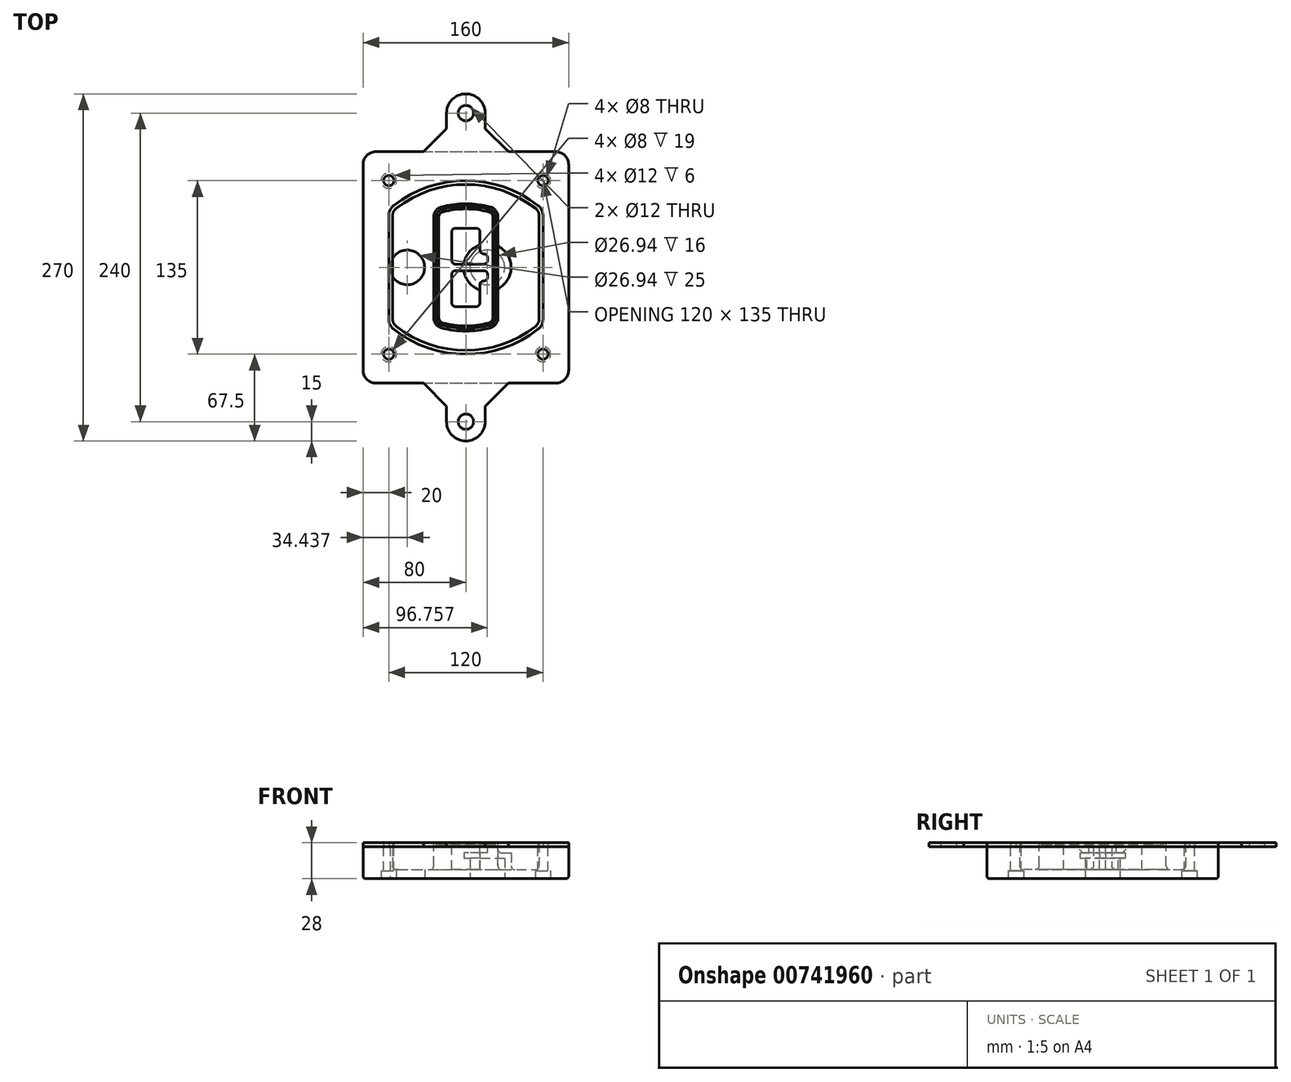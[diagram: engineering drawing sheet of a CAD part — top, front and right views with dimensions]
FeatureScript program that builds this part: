
annotation { "Feature Type Name" : "Feature", "Feature Type Description" : "" }
export const myFeature = defineFeature(function(context is Context, id is Id, definition is map)
    precondition{}
    {
        {
            var Q0;
            Q0=qCreatedBy(makeId("Top.planeOp"),FACE);
            var sketch = newSketch(context, id + "F0", { "sketchPlane" : qUnion([Q0])});
            skPoint(sketch, "E0.rect.middle", {"position": v(0, 0) * mm});
            skLineSegment(sketch, "E1.bottom", {"start": v(-70, -90) * mm, "end": v(70, -90) * mm});
            skLineSegment(sketch, "E1.top", {"start": v(-70, 90) * mm, "end": v(70, 90) * mm});
            skLineSegment(sketch, "E1.left", {"start": v(-80, -80) * mm, "end": v(-80, 80) * mm});
            skLineSegment(sketch, "E1.right", {"start": v(80, -80) * mm, "end": v(80, 80) * mm});
            skLineSegment(sketch, "E2", {"start": v(-80, 90) * mm, "end": v(80, -90) * mm, "construction": true});
            skLineSegment(sketch, "E3", {"start": v(80, 90) * mm, "end": v(-80, -90) * mm, "construction": true});
            skCircle(sketch, "E4", {"center": v(-60, 67.5) * mm, "radius": 4 * mm});
            skCircle(sketch, "E5", {"center": v(60, 67.5) * mm, "radius": 4 * mm});
            skCircle(sketch, "E6", {"center": v(60, -67.5) * mm, "radius": 4 * mm});
            skCircle(sketch, "E7", {"center": v(-60, -67.5) * mm, "radius": 4 * mm});
            skLineSegment(sketch, "E8", {"start": v(-60, 67.5) * mm, "end": v(60, 67.5) * mm, "construction": true});
            skLineSegment(sketch, "E9", {"start": v(60, 67.5) * mm, "end": v(60, -67.5) * mm, "construction": true});
            skLineSegment(sketch, "E10", {"start": v(60, -67.5) * mm, "end": v(-60, -67.5) * mm, "construction": true});
            skLineSegment(sketch, "E11", {"start": v(-60, -67.5) * mm, "end": v(-60, 67.5) * mm, "construction": true});
            skLineSegment(sketch, "E12", {"start": v(-60, 40.3) * mm, "end": v(-60, -40.3) * mm});
            skLineSegment(sketch, "E13", {"start": v(60, 40.3) * mm, "end": v(60, -40.3) * mm});
            skArc(sketch, "E14", {"start": v(56.15, 48.18) * mm, "mid": v(0, 67.5) * mm, "end": v(-56.15, 48.18) * mm});
            skArc(sketch, "E15", {"start": v(-56.15, -48.18) * mm, "mid": v(0, -67.5) * mm, "end": v(56.15, -48.18) * mm});
            skLineSegment(sketch, "E16", {"start": v(-60, 0) * mm, "end": v(60, 0) * mm, "construction": true});
            skPoint(sketch, "E17.visualSharp", {"position": v(-60, -45) * mm});
            skArc(sketch, "E17.filletArc", {"start": v(-60, -40.3) * mm, "mid": v(-58.99, -44.68) * mm, "end": v(-56.15, -48.18) * mm});
            skPoint(sketch, "E18.visualSharp", {"position": v(-60, 45) * mm});
            skArc(sketch, "E18.filletArc", {"start": v(-56.15, 48.18) * mm, "mid": v(-58.99, 44.68) * mm, "end": v(-60, 40.3) * mm});
            skPoint(sketch, "E19.visualSharp", {"position": v(60, 45) * mm});
            skArc(sketch, "E19.filletArc", {"start": v(60, 40.3) * mm, "mid": v(58.99, 44.68) * mm, "end": v(56.15, 48.18) * mm});
            skPoint(sketch, "E20.visualSharp", {"position": v(60, -45) * mm});
            skArc(sketch, "E20.filletArc", {"start": v(56.15, -48.18) * mm, "mid": v(58.99, -44.68) * mm, "end": v(60, -40.3) * mm});
            skPoint(sketch, "E21.visualSharp", {"position": v(-80, 90) * mm});
            skArc(sketch, "E21.filletArc", {"start": v(-70, 90) * mm, "mid": v(-77.07, 87.07) * mm, "end": v(-80, 80) * mm});
            skPoint(sketch, "E22.visualSharp", {"position": v(80, 90) * mm});
            skArc(sketch, "E22.filletArc", {"start": v(80, 80) * mm, "mid": v(77.07, 87.07) * mm, "end": v(70, 90) * mm});
            skPoint(sketch, "E23.visualSharp", {"position": v(80, -90) * mm});
            skArc(sketch, "E23.filletArc", {"start": v(70, -90) * mm, "mid": v(77.07, -87.07) * mm, "end": v(80, -80) * mm});
            skPoint(sketch, "E24.visualSharp", {"position": v(-80, -90) * mm});
            skArc(sketch, "E24.filletArc", {"start": v(-80, -80) * mm, "mid": v(-77.07, -87.07) * mm, "end": v(-70, -90) * mm});
            skArc(sketch, "E25.0", {"start": v(57, 40.3) * mm, "mid": v(56.3, 43.36) * mm, "end": v(54.3, 45.81) * mm});
            skLineSegment(sketch, "E25.1", {"start": v(57, 40.3) * mm, "end": v(57, -40.3) * mm});
            skArc(sketch, "E25.2", {"start": v(54.3, -45.81) * mm, "mid": v(56.3, -43.36) * mm, "end": v(57, -40.3) * mm});
            skArc(sketch, "E25.3", {"start": v(-54.3, -45.81) * mm, "mid": v(0, -64.5) * mm, "end": v(54.3, -45.81) * mm});
            skArc(sketch, "E25.4", {"start": v(-57, -40.3) * mm, "mid": v(-56.3, -43.36) * mm, "end": v(-54.3, -45.81) * mm});
            skArc(sketch, "E25.5", {"start": v(54.3, 45.81) * mm, "mid": v(0, 64.5) * mm, "end": v(-54.3, 45.81) * mm});
            skLineSegment(sketch, "E25.6", {"start": v(-57, 40.3) * mm, "end": v(-57, -40.3) * mm});
            skArc(sketch, "E25.7", {"start": v(-54.3, 45.81) * mm, "mid": v(-56.3, 43.36) * mm, "end": v(-57, 40.3) * mm});
            skArc(sketch, "E26.0", {"start": v(-58.62, 51.33) * mm, "mid": v(-62.58, 46.43) * mm, "end": v(-64, 40.3) * mm});
            skArc(sketch, "E26.1", {"start": v(58.62, 51.33) * mm, "mid": v(0, 71.5) * mm, "end": v(-58.62, 51.33) * mm});
            skArc(sketch, "E26.2", {"start": v(64, 40.3) * mm, "mid": v(62.58, 46.43) * mm, "end": v(58.62, 51.33) * mm});
            skLineSegment(sketch, "E26.3", {"start": v(64, 40.3) * mm, "end": v(64, -40.3) * mm});
            skArc(sketch, "E26.4", {"start": v(58.62, -51.33) * mm, "mid": v(62.58, -46.43) * mm, "end": v(64, -40.3) * mm});
            skLineSegment(sketch, "E26.5", {"start": v(-64, 40.3) * mm, "end": v(-64, -40.3) * mm});
            skArc(sketch, "E26.6", {"start": v(-58.62, -51.33) * mm, "mid": v(0, -71.5) * mm, "end": v(58.62, -51.33) * mm});
            skArc(sketch, "E26.7", {"start": v(-64, -40.3) * mm, "mid": v(-62.58, -46.43) * mm, "end": v(-58.62, -51.33) * mm});
            skSolve(sketch);
        }
        {
            var Q0;
            Q0=makeQuery(id+"F0.imprint","IMPRINT",FACE,{"disambiguationData":[TD([[makeQuery(id+"F0.imprint","IMPRINT",EDGE,{"derivedFrom":sQuery(id+"F0.wireOp",EDGE,"E1.bottom")}),1.0]])]});
            var Q1;
            Q1=makeQuery(id+"F0.imprint","IMPRINT",FACE,{"disambiguationData":[TD([[makeQuery(id+"F0.imprint","IMPRINT",EDGE,{"derivedFrom":sQuery(id+"F0.wireOp",EDGE,"E12")}),1.0]])]});
            var Q2;
            Q2=makeQuery(id+"F0.imprint","IMPRINT",FACE,{"disambiguationData":[TD([[makeQuery(id+"F0.imprint","IMPRINT",EDGE,{"derivedFrom":sQuery(id+"F0.wireOp",EDGE,"E25.0")}),1.0]])]});
            var Q3;
            Q3=makeQuery(id+"F0.imprint","IMPRINT",FACE,{"disambiguationData":[TD([[makeQuery(id+"F0.imprint","IMPRINT",EDGE,{"derivedFrom":sQuery(id+"F0.wireOp",EDGE,"E12")}),-1.0]])]});
            extrude(context, id + "F1", {"entities" : qUnion([Q0, Q1, Q2, Q3]), "oppositeDirection" : true, "depth" : 25 * mm});
        }
        {
            var Q0;
            Q0=makeQuery(id+"F0.imprint","IMPRINT",FACE,{"disambiguationData":[TD([[makeQuery(id+"F0.imprint","IMPRINT",EDGE,{"derivedFrom":sQuery(id+"F0.wireOp",EDGE,"E12")}),1.0]])]});
            extrude(context, id + "F2", {"entities" : qUnion([Q0]), "operationType" : NewBodyOperationType.ADD, "depth" : 3 * mm});
        }
        {
            var Q0;
            Q0=makeQuery(id+"F0.imprint","IMPRINT",FACE,{"disambiguationData":[TD([[makeQuery(id+"F0.imprint","IMPRINT",EDGE,{"derivedFrom":sQuery(id+"F0.wireOp",EDGE,"E25.0")}),1.0]])]});
            extrude(context, id + "F3", {"entities" : qUnion([Q0]), "operationType" : NewBodyOperationType.REMOVE, "oppositeDirection" : true, "depth" : 18 * mm});
        }
        {
            var Q0;
            Q0=makeQuery(id+"F2.opExtrude","CAP_FACE",FACE,{"disambiguationData":[OSD([sQuery(id+"F0.wireOp",EDGE,"E12"),sQuery(id+"F0.wireOp",EDGE,"E13"),sQuery(id+"F0.wireOp",EDGE,"E14"),sQuery(id+"F0.wireOp",EDGE,"E15"),sQuery(id+"F0.wireOp",EDGE,"E17.filletArc"),sQuery(id+"F0.wireOp",EDGE,"E18.filletArc"),sQuery(id+"F0.wireOp",EDGE,"E19.filletArc"),sQuery(id+"F0.wireOp",EDGE,"E20.filletArc"),sQuery(id+"F0.wireOp",EDGE,"E25.0"),sQuery(id+"F0.wireOp",EDGE,"E25.1"),sQuery(id+"F0.wireOp",EDGE,"E25.2"),sQuery(id+"F0.wireOp",EDGE,"E25.3"),sQuery(id+"F0.wireOp",EDGE,"E25.4"),sQuery(id+"F0.wireOp",EDGE,"E25.5"),sQuery(id+"F0.wireOp",EDGE,"E25.6"),sQuery(id+"F0.wireOp",EDGE,"E25.7")])],"isStart":false});
            var sketch = newSketch(context, id + "F4", { "sketchPlane" : qUnion([Q0])});
            skArc(sketch, "E27.0", {"start": v(-19.08, -46.97) * mm, "mid": v(0, -49.5) * mm, "end": v(19.08, -46.97) * mm});
            skArc(sketch, "E28.0", {"start": v(19.08, 46.97) * mm, "mid": v(0, 49.5) * mm, "end": v(-19.08, 46.97) * mm});
            skLineSegment(sketch, "E29", {"start": v(-25, 39.25) * mm, "end": v(-25, -39.25) * mm});
            skLineSegment(sketch, "E30", {"start": v(25, 39.25) * mm, "end": v(25, -39.25) * mm});
            skLineSegment(sketch, "E31", {"start": v(-25, 45.1) * mm, "end": v(25, 45.1) * mm, "construction": true});
            skLineSegment(sketch, "E32", {"start": v(-25, -45.1) * mm, "end": v(25, -45.1) * mm, "construction": true});
            skPoint(sketch, "E33.visualSharp", {"position": v(-25, 45.1) * mm});
            skArc(sketch, "E33.filletArc", {"start": v(-19.08, 46.97) * mm, "mid": v(-23.35, 44.11) * mm, "end": v(-25, 39.25) * mm});
            skPoint(sketch, "E34.visualSharp", {"position": v(25, 45.1) * mm});
            skArc(sketch, "E34.filletArc", {"start": v(25, 39.25) * mm, "mid": v(23.35, 44.11) * mm, "end": v(19.08, 46.97) * mm});
            skPoint(sketch, "E35.visualSharp", {"position": v(25, -45.1) * mm});
            skArc(sketch, "E35.filletArc", {"start": v(19.08, -46.97) * mm, "mid": v(23.35, -44.11) * mm, "end": v(25, -39.25) * mm});
            skPoint(sketch, "E36.visualSharp", {"position": v(-25, -45.1) * mm});
            skArc(sketch, "E36.filletArc", {"start": v(-25, -39.25) * mm, "mid": v(-23.35, -44.11) * mm, "end": v(-19.08, -46.97) * mm});
            skArc(sketch, "E37.0", {"start": v(54.3, 45.81) * mm, "mid": v(0, 64.5) * mm, "end": v(-54.3, 45.81) * mm});
            skArc(sketch, "E37.1", {"start": v(-54.3, 45.81) * mm, "mid": v(-56.3, 43.36) * mm, "end": v(-57, 40.3) * mm});
            skLineSegment(sketch, "E37.2", {"start": v(-57, 40.3) * mm, "end": v(-57, -40.3) * mm});
            skArc(sketch, "E37.3", {"start": v(-57, -40.3) * mm, "mid": v(-56.3, -43.36) * mm, "end": v(-54.3, -45.81) * mm});
            skArc(sketch, "E37.4", {"start": v(-54.3, -45.81) * mm, "mid": v(0, -64.5) * mm, "end": v(54.3, -45.81) * mm});
            skArc(sketch, "E37.5", {"start": v(54.3, -45.81) * mm, "mid": v(56.3, -43.36) * mm, "end": v(57, -40.3) * mm});
            skLineSegment(sketch, "E37.6", {"start": v(57, 40.3) * mm, "end": v(57, -40.3) * mm});
            skArc(sketch, "E37.7", {"start": v(57, 40.3) * mm, "mid": v(56.3, 43.36) * mm, "end": v(54.3, 45.81) * mm});
            skLineSegment(sketch, "E38.0", {"start": v(23, 39.25) * mm, "end": v(23, -39.25) * mm});
            skArc(sketch, "E38.1", {"start": v(18.56, -45.04) * mm, "mid": v(21.76, -42.9) * mm, "end": v(23, -39.25) * mm});
            skArc(sketch, "E38.2", {"start": v(-18.56, -45.04) * mm, "mid": v(0, -47.5) * mm, "end": v(18.56, -45.04) * mm});
            skArc(sketch, "E38.3", {"start": v(-23, -39.25) * mm, "mid": v(-21.76, -42.9) * mm, "end": v(-18.56, -45.04) * mm});
            skLineSegment(sketch, "E38.4", {"start": v(-23, 39.25) * mm, "end": v(-23, -39.25) * mm});
            skArc(sketch, "E38.5", {"start": v(23, 39.25) * mm, "mid": v(21.76, 42.9) * mm, "end": v(18.56, 45.04) * mm});
            skArc(sketch, "E38.6", {"start": v(-18.56, 45.04) * mm, "mid": v(-21.76, 42.9) * mm, "end": v(-23, 39.25) * mm});
            skArc(sketch, "E38.7", {"start": v(18.56, 45.04) * mm, "mid": v(0, 47.5) * mm, "end": v(-18.56, 45.04) * mm});
            skArc(sketch, "E39.0", {"start": v(21, 39.25) * mm, "mid": v(20.18, 41.68) * mm, "end": v(18.04, 43.1) * mm});
            skLineSegment(sketch, "E39.1", {"start": v(21, 39.25) * mm, "end": v(21, -39.25) * mm});
            skArc(sketch, "E39.2", {"start": v(18.04, -43.1) * mm, "mid": v(20.18, -41.68) * mm, "end": v(21, -39.25) * mm});
            skArc(sketch, "E39.3", {"start": v(-18.04, -43.1) * mm, "mid": v(0, -45.5) * mm, "end": v(18.04, -43.1) * mm});
            skArc(sketch, "E39.4", {"start": v(-21, -39.25) * mm, "mid": v(-20.18, -41.68) * mm, "end": v(-18.04, -43.1) * mm});
            skArc(sketch, "E39.5", {"start": v(18.04, 43.1) * mm, "mid": v(0, 45.5) * mm, "end": v(-18.04, 43.1) * mm});
            skLineSegment(sketch, "E39.6", {"start": v(-21, 39.25) * mm, "end": v(-21, -39.25) * mm});
            skArc(sketch, "E39.7", {"start": v(-18.04, 43.1) * mm, "mid": v(-20.18, 41.68) * mm, "end": v(-21, 39.25) * mm});
            skLineSegment(sketch, "E40", {"start": v(-25, 0) * mm, "end": v(25, 0) * mm, "construction": true});
            skLineSegment(sketch, "E41", {"start": v(-11, 5.5) * mm, "end": v(-11, 27.5) * mm});
            skLineSegment(sketch, "E42", {"start": v(-8, 30.5) * mm, "end": v(8, 30.5) * mm});
            skLineSegment(sketch, "E43", {"start": v(11, 27.5) * mm, "end": v(11, 13.5) * mm});
            skLineSegment(sketch, "E44", {"start": v(14, 10.5) * mm, "end": v(14, 10.5) * mm});
            skLineSegment(sketch, "E45", {"start": v(17, 7.5) * mm, "end": v(17, 5.5) * mm});
            skLineSegment(sketch, "E46", {"start": v(14, 2.5) * mm, "end": v(-8, 2.5) * mm});
            skPoint(sketch, "E47.visualSharp", {"position": v(-11, 30.5) * mm});
            skArc(sketch, "E47.filletArc", {"start": v(-8, 30.5) * mm, "mid": v(-10.12, 29.62) * mm, "end": v(-11, 27.5) * mm});
            skPoint(sketch, "E48.visualSharp", {"position": v(11, 30.5) * mm});
            skArc(sketch, "E48.filletArc", {"start": v(11, 27.5) * mm, "mid": v(10.12, 29.62) * mm, "end": v(8, 30.5) * mm});
            skPoint(sketch, "E49.visualSharp", {"position": v(11, 10.5) * mm});
            skArc(sketch, "E49.filletArc", {"start": v(11, 13.5) * mm, "mid": v(11.88, 11.38) * mm, "end": v(14, 10.5) * mm});
            skPoint(sketch, "E50.visualSharp", {"position": v(17, 10.5) * mm});
            skArc(sketch, "E50.filletArc", {"start": v(17, 7.5) * mm, "mid": v(16.12, 9.62) * mm, "end": v(14, 10.5) * mm});
            skPoint(sketch, "E51.visualSharp", {"position": v(17, 2.5) * mm});
            skArc(sketch, "E51.filletArc", {"start": v(14, 2.5) * mm, "mid": v(16.12, 3.38) * mm, "end": v(17, 5.5) * mm});
            skPoint(sketch, "E52.visualSharp", {"position": v(-11, 2.5) * mm});
            skArc(sketch, "E52.filletArc", {"start": v(-11, 5.5) * mm, "mid": v(-10.12, 3.38) * mm, "end": v(-8, 2.5) * mm});
            skLineSegment(sketch, "E53.0.MirrorCS", {"start": v(14, -2.5) * mm, "end": v(-8, -2.5) * mm});
            skArc(sketch, "E54.0.MirrorCS", {"start": v(-11, -5.5) * mm, "mid": v(-10.12, -3.38) * mm, "end": v(-8, -2.5) * mm});
            skLineSegment(sketch, "E55.0.MirrorCS", {"start": v(-11, -5.5) * mm, "end": v(-11, -27.5) * mm});
            skArc(sketch, "E56.0.MirrorCS", {"start": v(-8, -30.5) * mm, "mid": v(-10.12, -29.62) * mm, "end": v(-11, -27.5) * mm});
            skLineSegment(sketch, "E57.0.MirrorCS", {"start": v(-8, -30.5) * mm, "end": v(8, -30.5) * mm});
            skArc(sketch, "E58.0.MirrorCS", {"start": v(11, -27.5) * mm, "mid": v(10.12, -29.62) * mm, "end": v(8, -30.5) * mm});
            skLineSegment(sketch, "E59.0.MirrorCS", {"start": v(11, -27.5) * mm, "end": v(11, -13.5) * mm});
            skArc(sketch, "E60.0.MirrorCS", {"start": v(11, -13.5) * mm, "mid": v(11.88, -11.38) * mm, "end": v(14, -10.5) * mm});
            skArc(sketch, "E61.0.MirrorCS", {"start": v(17, -7.5) * mm, "mid": v(16.12, -9.62) * mm, "end": v(14, -10.5) * mm});
            skLineSegment(sketch, "E62.0.MirrorCS", {"start": v(17, -7.5) * mm, "end": v(17, -5.5) * mm});
            skArc(sketch, "E63.0.MirrorCS", {"start": v(14, -2.5) * mm, "mid": v(16.12, -3.38) * mm, "end": v(17, -5.5) * mm});
            skSolve(sketch);
        }
        {
            var Q0;
            Q0=makeQuery(id+"F4.imprint","IMPRINT",FACE,{"disambiguationData":[TD([[makeQuery(id+"F4.imprint","IMPRINT",EDGE,{"derivedFrom":sQuery(id+"F4.wireOp",EDGE,"E27.0")}),1.0]])]});
            var Q1;
            Q1=makeQuery(id+"F4.imprint","IMPRINT",FACE,{"disambiguationData":[TD([[makeQuery(id+"F4.imprint","IMPRINT",EDGE,{"derivedFrom":sQuery(id+"F4.wireOp",EDGE,"E38.0")}),-1.0]])]});
            var Q2;
            Q2=makeQuery(id+"F4.imprint","IMPRINT",FACE,{"disambiguationData":[TD([[makeQuery(id+"F4.imprint","IMPRINT",EDGE,{"derivedFrom":sQuery(id+"F4.wireOp",EDGE,"E39.0")}),1.0]])]});
            extrude(context, id + "F5", {"entities" : qUnion([Q0, Q1, Q2]), "operationType" : NewBodyOperationType.ADD, "endBound" : BoundingType.UP_TO_NEXT, "oppositeDirection" : true, "depth" : 25 * mm});
        }
        {
            var Q0;
            Q0=makeQuery(id+"F4.imprint","IMPRINT",FACE,{"disambiguationData":[TD([[makeQuery(id+"F4.imprint","IMPRINT",EDGE,{"derivedFrom":sQuery(id+"F4.wireOp",EDGE,"E38.0")}),-1.0]])]});
            extrude(context, id + "F6", {"entities" : qUnion([Q0]), "operationType" : NewBodyOperationType.REMOVE, "oppositeDirection" : true, "depth" : 2 * mm});
        }
        {
            var Q0;
            Q0=makeQuery(id+"F1.opExtrude","CAP_FACE",FACE,{"disambiguationData":[OSD([sQuery(id+"F0.wireOp",EDGE,"E1.bottom"),sQuery(id+"F0.wireOp",EDGE,"E1.top"),sQuery(id+"F0.wireOp",EDGE,"E1.left"),sQuery(id+"F0.wireOp",EDGE,"E1.right"),sQuery(id+"F0.wireOp",EDGE,"E4"),sQuery(id+"F0.wireOp",EDGE,"E5"),sQuery(id+"F0.wireOp",EDGE,"E6"),sQuery(id+"F0.wireOp",EDGE,"E7"),sQuery(id+"F0.wireOp",EDGE,"E21.filletArc"),sQuery(id+"F0.wireOp",EDGE,"E22.filletArc"),sQuery(id+"F0.wireOp",EDGE,"E23.filletArc"),sQuery(id+"F0.wireOp",EDGE,"E24.filletArc")])],"isStart":false});
            var sketch = newSketch(context, id + "F7", { "sketchPlane" : qUnion([Q0])});
            skCircle(sketch, "E64", {"center": v(16.76, 0) * mm, "radius": 13.47 * mm});
            skCircle(sketch, "E65", {"center": v(-45.56, 0) * mm, "radius": 13.47 * mm});
            skLineSegment(sketch, "E66", {"start": v(80, 0) * mm, "end": v(-80, 0) * mm});
            skCircle(sketch, "E67", {"center": v(16.76, 0) * mm, "radius": 18.47 * mm});
            skCircle(sketch, "E68", {"center": v(60, -67.5) * mm, "radius": 6 * mm});
            skCircle(sketch, "E69", {"center": v(-60, -67.5) * mm, "radius": 6 * mm});
            skCircle(sketch, "E70", {"center": v(-60, 67.5) * mm, "radius": 6 * mm});
            skCircle(sketch, "E71", {"center": v(60, 67.5) * mm, "radius": 6 * mm});
            skSolve(sketch);
        }
        {
            var Q0;
            {var subQ1=sQuery(id+"F7.wireOp",EDGE,"E66");var subQ4=sQuery(id+"F7.wireOp",EDGE,"E64");var subQ6=makeQuery(id+"F7.imprint","INTERSECT",VERTEX,{"disambiguationData":[OD(0.0)],"derivedFrom":[subQ4,subQ1]});Q0=makeQuery(id+"F7.imprint","IMPRINT",FACE,{"disambiguationData":[TD([[makeQuery(id+"F7.imprint","IMPRINT",EDGE,{"disambiguationData":[TD([[subQ6,-1.0]])],"derivedFrom":subQ4}),-1.0]])]});}
            var Q1;
            {var subQ0=sQuery(id+"F7.wireOp",EDGE,"E66");var subQ1=sQuery(id+"F7.wireOp",EDGE,"E64");var subQ3=makeQuery(id+"F7.imprint","INTERSECT",VERTEX,{"disambiguationData":[OD(0.0)],"derivedFrom":[subQ1,subQ0]});Q1=makeQuery(id+"F7.imprint","IMPRINT",FACE,{"disambiguationData":[TD([[makeQuery(id+"F7.imprint","IMPRINT",EDGE,{"disambiguationData":[TD([[subQ3,-1.0]])],"derivedFrom":subQ1}),1.0]])]});}
            var Q2;
            {var subQ0=sQuery(id+"F7.wireOp",EDGE,"E66");var subQ1=sQuery(id+"F7.wireOp",EDGE,"E64");var subQ3=makeQuery(id+"F7.imprint","INTERSECT",VERTEX,{"disambiguationData":[OD(0.0)],"derivedFrom":[subQ1,subQ0]});Q2=makeQuery(id+"F7.imprint","IMPRINT",FACE,{"disambiguationData":[TD([[makeQuery(id+"F7.imprint","IMPRINT",EDGE,{"disambiguationData":[TD([[subQ3,1.0]])],"derivedFrom":subQ1}),1.0]])]});}
            var Q3;
            {var subQ1=sQuery(id+"F7.wireOp",EDGE,"E66");var subQ4=sQuery(id+"F7.wireOp",EDGE,"E64");var subQ6=makeQuery(id+"F7.imprint","INTERSECT",VERTEX,{"disambiguationData":[OD(0.0)],"derivedFrom":[subQ4,subQ1]});Q3=makeQuery(id+"F7.imprint","IMPRINT",FACE,{"disambiguationData":[TD([[makeQuery(id+"F7.imprint","IMPRINT",EDGE,{"disambiguationData":[TD([[subQ6,1.0]])],"derivedFrom":subQ4}),-1.0]])]});}
            extrude(context, id + "F8", {"entities" : qUnion([Q0, Q1, Q2, Q3]), "operationType" : NewBodyOperationType.ADD, "oppositeDirection" : true, "depth" : 20 * mm});
        }
        {
            var Q0;
            {var subQ0=sQuery(id+"F7.wireOp",EDGE,"E66");var subQ1=sQuery(id+"F7.wireOp",EDGE,"E64");var subQ3=makeQuery(id+"F7.imprint","INTERSECT",VERTEX,{"disambiguationData":[OD(0.0)],"derivedFrom":[subQ1,subQ0]});Q0=makeQuery(id+"F7.imprint","IMPRINT",FACE,{"disambiguationData":[TD([[makeQuery(id+"F7.imprint","IMPRINT",EDGE,{"disambiguationData":[TD([[subQ3,-1.0]])],"derivedFrom":subQ1}),1.0]])]});}
            var Q1;
            {var subQ0=sQuery(id+"F7.wireOp",EDGE,"E66");var subQ1=sQuery(id+"F7.wireOp",EDGE,"E64");var subQ3=makeQuery(id+"F7.imprint","INTERSECT",VERTEX,{"disambiguationData":[OD(0.0)],"derivedFrom":[subQ1,subQ0]});Q1=makeQuery(id+"F7.imprint","IMPRINT",FACE,{"disambiguationData":[TD([[makeQuery(id+"F7.imprint","IMPRINT",EDGE,{"disambiguationData":[TD([[subQ3,1.0]])],"derivedFrom":subQ1}),1.0]])]});}
            extrude(context, id + "F9", {"entities" : qUnion([Q0, Q1]), "operationType" : NewBodyOperationType.REMOVE, "oppositeDirection" : true, "depth" : 16 * mm});
        }
        {
            var Q0;
            {var subQ0=sQuery(id+"F7.wireOp",EDGE,"E66");var subQ1=sQuery(id+"F7.wireOp",EDGE,"E65");var subQ3=makeQuery(id+"F7.imprint","INTERSECT",VERTEX,{"disambiguationData":[OD(0.0)],"derivedFrom":[subQ1,subQ0]});Q0=makeQuery(id+"F7.imprint","IMPRINT",FACE,{"disambiguationData":[TD([[makeQuery(id+"F7.imprint","IMPRINT",EDGE,{"disambiguationData":[TD([[subQ3,-1.0]])],"derivedFrom":subQ1}),1.0]])]});}
            var Q1;
            {var subQ0=sQuery(id+"F7.wireOp",EDGE,"E66");var subQ1=sQuery(id+"F7.wireOp",EDGE,"E65");var subQ3=makeQuery(id+"F7.imprint","INTERSECT",VERTEX,{"disambiguationData":[OD(0.0)],"derivedFrom":[subQ1,subQ0]});Q1=makeQuery(id+"F7.imprint","IMPRINT",FACE,{"disambiguationData":[TD([[makeQuery(id+"F7.imprint","IMPRINT",EDGE,{"disambiguationData":[TD([[subQ3,1.0]])],"derivedFrom":subQ1}),1.0]])]});}
            extrude(context, id + "F10", {"entities" : qUnion([Q0, Q1]), "operationType" : NewBodyOperationType.REMOVE, "oppositeDirection" : true, "depth" : 25 * mm});
        }
        {
            var Q0;
            Q0=makeQuery(id+"F7.imprint","IMPRINT",FACE,{"disambiguationData":[TD([[makeQuery(id+"F7.imprint","IMPRINT",EDGE,{"derivedFrom":sQuery(id+"F7.wireOp",EDGE,"E68")}),1.0]])]});
            var Q1;
            Q1=makeQuery(id+"F7.imprint","IMPRINT",FACE,{"disambiguationData":[TD([[makeQuery(id+"F7.imprint","IMPRINT",EDGE,{"derivedFrom":makeQuery(id+"F1.opExtrude","CAP_EDGE",EDGE,{"disambiguationData":[OSD([sQuery(id+"F0.wireOp",EDGE,"E5")])],"isStart":false})}),-1.0]])]});
            var Q2;
            Q2=makeQuery(id+"F7.imprint","IMPRINT",FACE,{"disambiguationData":[TD([[makeQuery(id+"F7.imprint","IMPRINT",EDGE,{"derivedFrom":sQuery(id+"F7.wireOp",EDGE,"E69")}),1.0]])]});
            var Q3;
            Q3=makeQuery(id+"F7.imprint","IMPRINT",FACE,{"disambiguationData":[TD([[makeQuery(id+"F7.imprint","IMPRINT",EDGE,{"derivedFrom":makeQuery(id+"F1.opExtrude","CAP_EDGE",EDGE,{"disambiguationData":[OSD([sQuery(id+"F0.wireOp",EDGE,"E4")])],"isStart":false})}),-1.0]])]});
            var Q4;
            Q4=makeQuery(id+"F7.imprint","IMPRINT",FACE,{"disambiguationData":[TD([[makeQuery(id+"F7.imprint","IMPRINT",EDGE,{"derivedFrom":sQuery(id+"F7.wireOp",EDGE,"E70")}),1.0]])]});
            var Q5;
            Q5=makeQuery(id+"F7.imprint","IMPRINT",FACE,{"disambiguationData":[TD([[makeQuery(id+"F7.imprint","IMPRINT",EDGE,{"derivedFrom":makeQuery(id+"F1.opExtrude","CAP_EDGE",EDGE,{"disambiguationData":[OSD([sQuery(id+"F0.wireOp",EDGE,"E7")])],"isStart":false})}),-1.0]])]});
            var Q6;
            Q6=makeQuery(id+"F7.imprint","IMPRINT",FACE,{"disambiguationData":[TD([[makeQuery(id+"F7.imprint","IMPRINT",EDGE,{"derivedFrom":sQuery(id+"F7.wireOp",EDGE,"E71")}),1.0]])]});
            var Q7;
            Q7=makeQuery(id+"F7.imprint","IMPRINT",FACE,{"disambiguationData":[TD([[makeQuery(id+"F7.imprint","IMPRINT",EDGE,{"derivedFrom":makeQuery(id+"F1.opExtrude","CAP_EDGE",EDGE,{"disambiguationData":[OSD([sQuery(id+"F0.wireOp",EDGE,"E6")])],"isStart":false})}),-1.0]])]});
            extrude(context, id + "F11", {"entities" : qUnion([Q0, Q1, Q2, Q3, Q4, Q5, Q6, Q7]), "operationType" : NewBodyOperationType.REMOVE, "oppositeDirection" : true, "depth" : 6 * mm});
        }
        {
            var Q0;
            Q0=makeQuery(id+"F9.boolean.opBoolean","COPY",FACE,{"derivedFrom":makeQuery(id+"F9.opExtrude","CAP_FACE",FACE,{"disambiguationData":[OSD([sQuery(id+"F7.wireOp",EDGE,"E64")])],"isStart":false})});
            var sketch = newSketch(context, id + "F12", { "sketchPlane" : qUnion([Q0])});
            skArc(sketch, "E72.0", {"start": v(11, 17.55) * mm, "mid": v(2.57, 11.82) * mm, "end": v(-1.54, 2.5) * mm});
            skArc(sketch, "E72.1", {"start": v(-1.54, -2.5) * mm, "mid": v(2.57, -11.82) * mm, "end": v(11, -17.55) * mm});
            skLineSegment(sketch, "E73", {"start": v(-1.54, -2.5) * mm, "end": v(14, -2.5) * mm});
            skLineSegment(sketch, "E74.0", {"start": v(14, 2.5) * mm, "end": v(-1.54, 2.5) * mm});
            skArc(sketch, "E74.1", {"start": v(14, 2.5) * mm, "mid": v(16.12, 3.38) * mm, "end": v(17, 5.5) * mm});
            skLineSegment(sketch, "E74.2", {"start": v(17, 7.5) * mm, "end": v(17, 5.5) * mm});
            skArc(sketch, "E74.3", {"start": v(17, 7.5) * mm, "mid": v(16.12, 9.62) * mm, "end": v(14, 10.5) * mm});
            skArc(sketch, "E74.4", {"start": v(11, 13.5) * mm, "mid": v(11.88, 11.38) * mm, "end": v(14, 10.5) * mm});
            skLineSegment(sketch, "E74.5", {"start": v(11, 17.55) * mm, "end": v(11, 13.5) * mm});
            skLineSegment(sketch, "E74.7", {"start": v(14, -2.5) * mm, "end": v(-1.54, -2.5) * mm});
            skArc(sketch, "E74.8", {"start": v(14, -2.5) * mm, "mid": v(16.12, -3.38) * mm, "end": v(17, -5.5) * mm});
            skLineSegment(sketch, "E74.9", {"start": v(17, -7.5) * mm, "end": v(17, -5.5) * mm});
            skArc(sketch, "E74.10", {"start": v(17, -7.5) * mm, "mid": v(16.12, -9.62) * mm, "end": v(14, -10.5) * mm});
            skArc(sketch, "E74.11", {"start": v(11, -13.5) * mm, "mid": v(11.88, -11.38) * mm, "end": v(14, -10.5) * mm});
            skLineSegment(sketch, "E74.12", {"start": v(11, -17.55) * mm, "end": v(11, -13.5) * mm});
            skPoint(sketch, "E75.orphan", {"position": v(11, -27.5) * mm});
            skPoint(sketch, "E76.orphan", {"position": v(-8, -2.5) * mm});
            skPoint(sketch, "E77.orphan", {"position": v(-8, 2.5) * mm});
            skPoint(sketch, "E78.orphan", {"position": v(11, 27.5) * mm});
            skSolve(sketch);
        }
        {
            var Q0;
            {var subQ7=sQuery(id+"F12.wireOp",EDGE,"E72.0");var subQ14=sQuery(id+"F12.wireOp",EDGE,"E72.1");var subQ16=sQuery(id+"F12.wireOp",EDGE,"E74.1");var subQ18=sQuery(id+"F12.wireOp",EDGE,"E74.8");Q0=qUnion([makeQuery(id+"F12.imprint","IMPRINT",FACE,{"disambiguationData":[TD([[makeQuery(id+"F12.imprint","IMPRINT",EDGE,{"derivedFrom":subQ7}),1.0]])]}),makeQuery(id+"F12.imprint","IMPRINT",FACE,{"disambiguationData":[TD([[makeQuery(id+"F12.imprint","IMPRINT",EDGE,{"derivedFrom":subQ14}),1.0]])]}),makeQuery(id+"F12.imprint","IMPRINT",FACE,{"disambiguationData":[TD([[makeQuery(id+"F12.imprint","IMPRINT",EDGE,{"derivedFrom":subQ16}),1.0]])]}),makeQuery(id+"F12.imprint","IMPRINT",FACE,{"disambiguationData":[TD([[makeQuery(id+"F12.imprint","IMPRINT",EDGE,{"derivedFrom":subQ18}),-1.0]])]})]);}
            var Q1;
            Q1=makeQuery(id+"F5.boolean.opBoolean","SPLIT",FACE,{"disambiguationData":[TD([makeQuery(id+"F5.opExtrude","SWEPT_FACE",FACE,{"disambiguationData":[OSD([sQuery(id+"F4.wireOp",EDGE,"E41")])]})])],"derivedFrom":makeQuery(id+"F3.boolean.opBoolean","COPY",FACE,{"derivedFrom":makeQuery(id+"F3.opExtrude","CAP_FACE",FACE,{"disambiguationData":[OSD([sQuery(id+"F0.wireOp",EDGE,"E25.0"),sQuery(id+"F0.wireOp",EDGE,"E25.1"),sQuery(id+"F0.wireOp",EDGE,"E25.2"),sQuery(id+"F0.wireOp",EDGE,"E25.3"),sQuery(id+"F0.wireOp",EDGE,"E25.4"),sQuery(id+"F0.wireOp",EDGE,"E25.5"),sQuery(id+"F0.wireOp",EDGE,"E25.6"),sQuery(id+"F0.wireOp",EDGE,"E25.7")])],"isStart":false})})});
            extrude(context, id + "F13", {"entities" : qUnion([Q0]), "operationType" : NewBodyOperationType.REMOVE, "endBound" : BoundingType.UP_TO_SURFACE, "endBoundEntityFace" : qUnion([Q1]), "depth" : 25 * mm});
        }
        {
            var Q0;
            Q0=makeQuery(id+"F3.boolean.opBoolean","COPY",EDGE,{"derivedFrom":makeQuery(id+"F3.opExtrude","CAP_EDGE",EDGE,{"disambiguationData":[OSD([sQuery(id+"F0.wireOp",EDGE,"E25.6")])],"isStart":false})});
            var Q1;
            Q1=makeQuery(id+"F8.boolean.opBoolean","INTERSECT",EDGE,{"derivedFrom":[makeQuery(id+"F5.opExtrude","SWEPT_FACE",FACE,{"disambiguationData":[OSD([sQuery(id+"F4.wireOp",EDGE,"E30")])]}),makeQuery(id+"F8.opExtrude","CAP_FACE",FACE,{"disambiguationData":[OSD([sQuery(id+"F7.wireOp",EDGE,"E67")])],"isStart":false})]});
            var Q2;
            Q2=makeQuery(id+"F8.boolean.opBoolean","INTERSECT",EDGE,{"disambiguationData":[OD(1.0)],"derivedFrom":[makeQuery(id+"F5.opExtrude","SWEPT_FACE",FACE,{"disambiguationData":[OSD([sQuery(id+"F4.wireOp",EDGE,"E30")])]}),makeQuery(id+"F8.opExtrude","SWEPT_FACE",FACE,{"disambiguationData":[OSD([sQuery(id+"F7.wireOp",EDGE,"E67")])]})]});
            var Q3;
            {var subQ0=sQuery(id+"F4.wireOp",EDGE,"E30");Q3=makeQuery(id+"F8.boolean.opBoolean","SPLIT",EDGE,{"disambiguationData":[TD([makeQuery(id+"F5.opExtrude","SWEPT_FACE",FACE,{"disambiguationData":[OSD([sQuery(id+"F4.wireOp",EDGE,"E35.filletArc")])]})])],"derivedFrom":makeQuery(id+"F5.opExtrude","CAP_EDGE",EDGE,{"disambiguationData":[OSD([subQ0])],"isStart":false})});}
            var Q4;
            {var subQ0=sQuery(id+"F0.wireOp",EDGE,"E25.7");var subQ1=sQuery(id+"F0.wireOp",EDGE,"E25.1");var subQ2=sQuery(id+"F0.wireOp",EDGE,"E25.6");var subQ3=sQuery(id+"F0.wireOp",EDGE,"E25.5");var subQ4=sQuery(id+"F0.wireOp",EDGE,"E25.4");var subQ5=sQuery(id+"F0.wireOp",EDGE,"E25.0");var subQ6=sQuery(id+"F0.wireOp",EDGE,"E25.2");var subQ7=sQuery(id+"F0.wireOp",EDGE,"E25.3");Q4=makeQuery(id+"F8.boolean.opBoolean","INTERSECT",EDGE,{"derivedFrom":[makeQuery(id+"F5.boolean.opBoolean","SPLIT",FACE,{"disambiguationData":[TD([makeQuery(id+"F2.opExtrude","SWEPT_FACE",FACE,{"disambiguationData":[OSD([subQ5])]})])],"derivedFrom":makeQuery(id+"F3.boolean.opBoolean","COPY",FACE,{"derivedFrom":makeQuery(id+"F3.opExtrude","CAP_FACE",FACE,{"disambiguationData":[OSD([subQ5,subQ1,subQ6,subQ7,subQ4,subQ3,subQ2,subQ0])],"isStart":false})})}),makeQuery(id+"F8.opExtrude","SWEPT_FACE",FACE,{"disambiguationData":[OSD([sQuery(id+"F7.wireOp",EDGE,"E67")])]})]});}
            var Q5;
            Q5=makeQuery(id+"F8.boolean.opBoolean","INTERSECT",EDGE,{"disambiguationData":[OD(0.0)],"derivedFrom":[makeQuery(id+"F5.opExtrude","SWEPT_FACE",FACE,{"disambiguationData":[OSD([sQuery(id+"F4.wireOp",EDGE,"E30")])]}),makeQuery(id+"F8.opExtrude","SWEPT_FACE",FACE,{"disambiguationData":[OSD([sQuery(id+"F7.wireOp",EDGE,"E67")])]})]});
            fillet(context, id + "F14", {"entities" : qUnion([Q0, Q1, Q2, Q3, Q4, Q5]), "radius" : 3 * mm, "tangentPropagation" : true, "allowEdgeOverflow" : false});
        }
        {
            var Q0;
            Q0=makeQuery(id+"F1.opExtrude","CAP_EDGE",EDGE,{"disambiguationData":[OSD([sQuery(id+"F0.wireOp",EDGE,"E1.bottom")])],"isStart":false});
            fillet(context, id + "F15", {"entities" : qUnion([Q0]), "radius" : 2 * mm, "tangentPropagation" : true, "allowEdgeOverflow" : false});
        }
        {
            var Q0;
            {var subQ0=sQuery(id+"F0.wireOp",EDGE,"E21.filletArc");var subQ1=sQuery(id+"F0.wireOp",EDGE,"E7");var subQ2=sQuery(id+"F0.wireOp",EDGE,"E6");var subQ3=sQuery(id+"F0.wireOp",EDGE,"E5");var subQ4=sQuery(id+"F0.wireOp",EDGE,"E4");var subQ5=sQuery(id+"F0.wireOp",EDGE,"E22.filletArc");var subQ6=sQuery(id+"F0.wireOp",EDGE,"E1.bottom");var subQ7=sQuery(id+"F0.wireOp",EDGE,"E1.right");var subQ8=sQuery(id+"F0.wireOp",EDGE,"E1.top");var subQ9=sQuery(id+"F0.wireOp",EDGE,"E1.left");var subQ10=sQuery(id+"F0.wireOp",EDGE,"E23.filletArc");var subQ11=sQuery(id+"F0.wireOp",EDGE,"E24.filletArc");Q0=makeQuery(id+"F2.boolean.opBoolean","SPLIT",FACE,{"disambiguationData":[TD([makeQuery(id+"F1.opExtrude","SWEPT_FACE",FACE,{"disambiguationData":[OSD([subQ6])]})])],"derivedFrom":makeQuery(id+"F1.opExtrude","CAP_FACE",FACE,{"disambiguationData":[OSD([subQ6,subQ8,subQ9,subQ7,subQ4,subQ3,subQ2,subQ1,subQ0,subQ5,subQ10,subQ11])],"isStart":true})});}
            var sketch = newSketch(context, id + "F16", { "sketchPlane" : qUnion([Q0])});
            skLineSegment(sketch, "E79.0", {"start": v(-70, 90) * mm, "end": v(70, 90) * mm});
            skArc(sketch, "E79.1", {"start": v(-70, 90) * mm, "mid": v(-77.07, 87.07) * mm, "end": v(-80, 80) * mm});
            skLineSegment(sketch, "E79.2", {"start": v(-80, -80) * mm, "end": v(-80, 80) * mm});
            skCircle(sketch, "E79.3", {"center": v(-60, 67.5) * mm, "radius": 4 * mm});
            skArc(sketch, "E79.4", {"start": v(80, 80) * mm, "mid": v(77.07, 87.07) * mm, "end": v(70, 90) * mm});
            skLineSegment(sketch, "E79.5", {"start": v(80, -80) * mm, "end": v(80, 80) * mm});
            skArc(sketch, "E79.6", {"start": v(70, -90) * mm, "mid": v(77.07, -87.07) * mm, "end": v(80, -80) * mm});
            skLineSegment(sketch, "E79.7", {"start": v(-70, -90) * mm, "end": v(70, -90) * mm});
            skArc(sketch, "E79.8", {"start": v(-80, -80) * mm, "mid": v(-77.07, -87.07) * mm, "end": v(-70, -90) * mm});
            skCircle(sketch, "E79.9", {"center": v(-60, -67.5) * mm, "radius": 4 * mm});
            skCircle(sketch, "E79.10", {"center": v(60, -67.5) * mm, "radius": 4 * mm});
            skCircle(sketch, "E79.11", {"center": v(60, 67.5) * mm, "radius": 4 * mm});
            skArc(sketch, "E79.12", {"start": v(56.15, 48.18) * mm, "mid": v(0, 67.5) * mm, "end": v(-56.15, 48.18) * mm});
            skArc(sketch, "E79.13", {"start": v(60, 40.3) * mm, "mid": v(58.99, 44.68) * mm, "end": v(56.15, 48.18) * mm});
            skLineSegment(sketch, "E79.14", {"start": v(60, 40.3) * mm, "end": v(60, -40.3) * mm});
            skArc(sketch, "E79.15", {"start": v(56.15, -48.18) * mm, "mid": v(58.99, -44.68) * mm, "end": v(60, -40.3) * mm});
            skArc(sketch, "E79.16", {"start": v(-56.15, -48.18) * mm, "mid": v(0, -67.5) * mm, "end": v(56.15, -48.18) * mm});
            skLineSegment(sketch, "E79.17", {"start": v(-60, 40.3) * mm, "end": v(-60, -40.3) * mm});
            skArc(sketch, "E79.18", {"start": v(-56.15, 48.18) * mm, "mid": v(-58.99, 44.68) * mm, "end": v(-60, 40.3) * mm});
            skArc(sketch, "E79.19", {"start": v(-60, -40.3) * mm, "mid": v(-58.99, -44.68) * mm, "end": v(-56.15, -48.18) * mm});
            skPoint(sketch, "E79.20", {"position": v(-58.99, -44.68) * mm});
            skLineSegment(sketch, "E80", {"start": v(-33, 90) * mm, "end": v(-15, 108) * mm});
            skLineSegment(sketch, "E81", {"start": v(-15, 108) * mm, "end": v(-15, 120) * mm});
            skLineSegment(sketch, "E82", {"start": v(33, 90) * mm, "end": v(15, 108) * mm});
            skLineSegment(sketch, "E83", {"start": v(15, 108) * mm, "end": v(15, 120) * mm});
            skArc(sketch, "E84", {"start": v(15, 120) * mm, "mid": v(0, 135) * mm, "end": v(-15, 120) * mm});
            skLineSegment(sketch, "E85", {"start": v(0, 120) * mm, "end": v(0, 90) * mm, "construction": true});
            skCircle(sketch, "E86", {"center": v(0, 120) * mm, "radius": 6 * mm});
            skLineSegment(sketch, "E87", {"start": v(-80, 0) * mm, "end": v(80, 0) * mm, "construction": true});
            skLineSegment(sketch, "E88.MirrorCS", {"start": v(-33, -90) * mm, "end": v(-15, -108) * mm});
            skLineSegment(sketch, "E89.MirrorCS", {"start": v(0, -120) * mm, "end": v(0, -90) * mm, "construction": true});
            skLineSegment(sketch, "E90.MirrorCS", {"start": v(-15, -108) * mm, "end": v(-15, -120) * mm});
            skArc(sketch, "E91.MirrorCS", {"start": v(15, -120) * mm, "mid": v(0, -135) * mm, "end": v(-15, -120) * mm});
            skCircle(sketch, "E92.MirrorC", {"center": v(0, -120) * mm, "radius": 6 * mm});
            skLineSegment(sketch, "E93.MirrorCS", {"start": v(15, -108) * mm, "end": v(15, -120) * mm});
            skLineSegment(sketch, "E94.MirrorCS", {"start": v(33, -90) * mm, "end": v(15, -108) * mm});
            skSolve(sketch);
        }
        {
            var Q0;
            {var subQ5=sQuery(id+"F16.wireOp",EDGE,"E79.1");Q0=makeQuery(id+"F16.imprint","IMPRINT",FACE,{"disambiguationData":[TD([[makeQuery(id+"F16.imprint","IMPRINT",EDGE,{"derivedFrom":subQ5}),1.0]])]});}
            var Q1;
            {var subQ0=sQuery(id+"F16.wireOp",EDGE,"E80");Q1=makeQuery(id+"F16.imprint","IMPRINT",FACE,{"disambiguationData":[TD([[makeQuery(id+"F16.imprint","IMPRINT",EDGE,{"derivedFrom":subQ0}),-1.0]])]});}
            var Q2;
            {var subQ0=sQuery(id+"F16.wireOp",EDGE,"E88.MirrorCS");Q2=makeQuery(id+"F16.imprint","IMPRINT",FACE,{"disambiguationData":[TD([[makeQuery(id+"F16.imprint","IMPRINT",EDGE,{"derivedFrom":subQ0}),1.0]])]});}
            var Q3;
            Q3=makeQuery(id+"F2.opExtrude","CAP_FACE",FACE,{"disambiguationData":[OSD([sQuery(id+"F0.wireOp",EDGE,"E12"),sQuery(id+"F0.wireOp",EDGE,"E13"),sQuery(id+"F0.wireOp",EDGE,"E14"),sQuery(id+"F0.wireOp",EDGE,"E15"),sQuery(id+"F0.wireOp",EDGE,"E17.filletArc"),sQuery(id+"F0.wireOp",EDGE,"E18.filletArc"),sQuery(id+"F0.wireOp",EDGE,"E19.filletArc"),sQuery(id+"F0.wireOp",EDGE,"E20.filletArc"),sQuery(id+"F0.wireOp",EDGE,"E25.0"),sQuery(id+"F0.wireOp",EDGE,"E25.1"),sQuery(id+"F0.wireOp",EDGE,"E25.2"),sQuery(id+"F0.wireOp",EDGE,"E25.3"),sQuery(id+"F0.wireOp",EDGE,"E25.4"),sQuery(id+"F0.wireOp",EDGE,"E25.5"),sQuery(id+"F0.wireOp",EDGE,"E25.6"),sQuery(id+"F0.wireOp",EDGE,"E25.7")])],"isStart":false});
            extrude(context, id + "F17", {"entities" : qUnion([Q0, Q1, Q2]), "endBound" : BoundingType.UP_TO_SURFACE, "depth" : 25 * mm, "endBoundEntityFace" : qUnion([Q3]), "offsetDistance" : 25 * mm});
        }
    });
